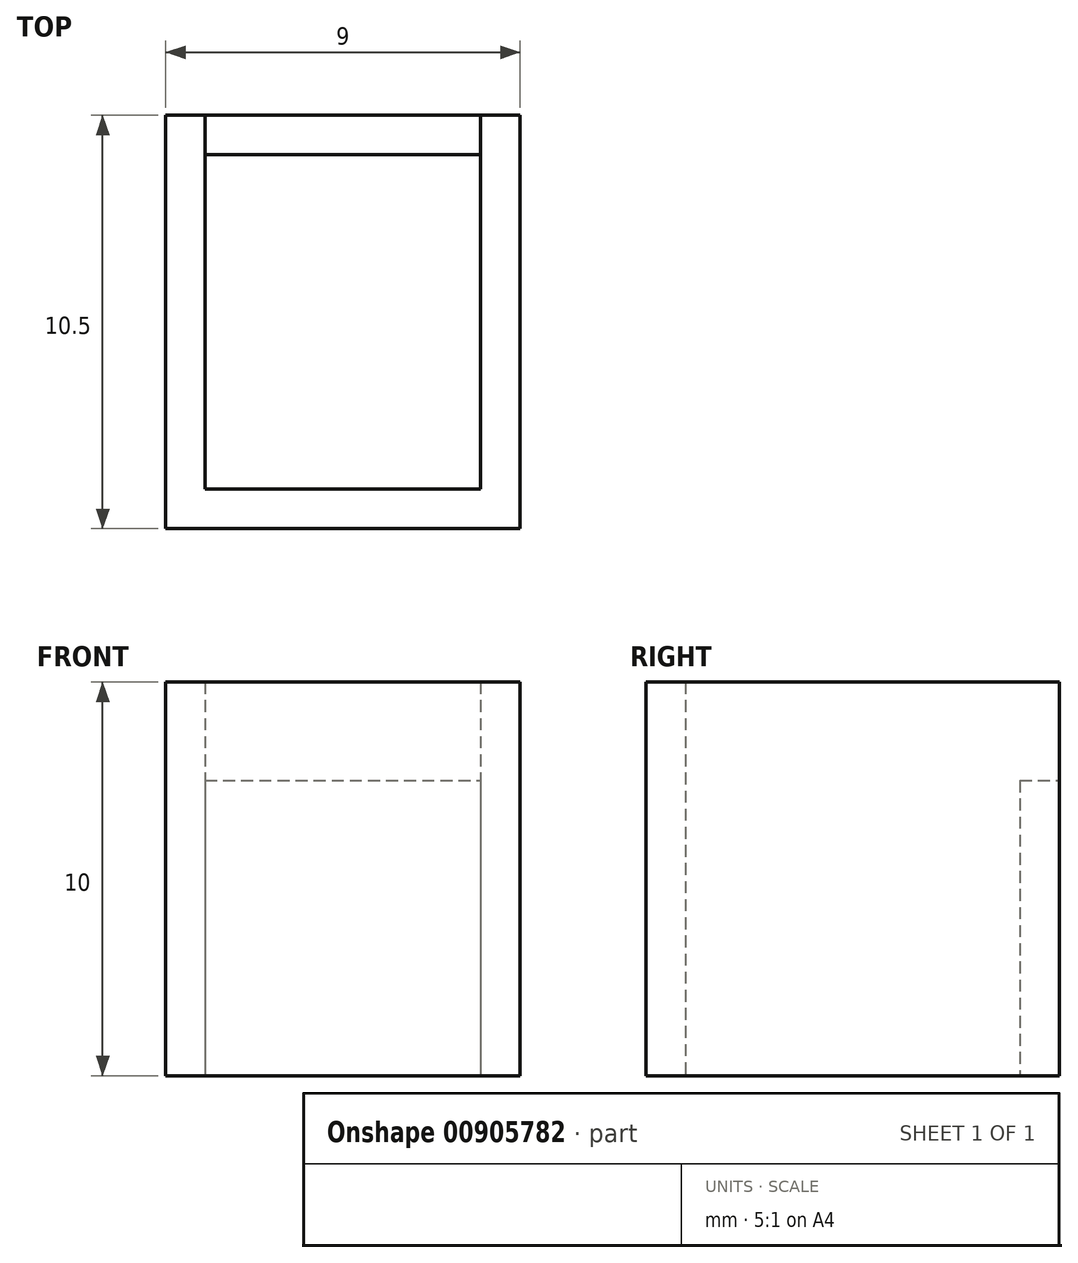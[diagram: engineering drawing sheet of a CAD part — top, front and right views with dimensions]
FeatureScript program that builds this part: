
annotation { "Feature Type Name" : "Feature", "Feature Type Description" : "" }
export const myFeature = defineFeature(function(context is Context, id is Id, definition is map)
    precondition{}
    {
        {
            var Q0;
            Q0=qCreatedBy(makeId("Top.planeOp"),FACE);
            var sketch = newSketch(context, id + "F0", { "sketchPlane" : qUnion([Q0])});
            skLineSegment(sketch, "E0.bottom", {"start": v(-3.5, 4.25) * mm, "end": v(3.5, 4.25) * mm});
            skLineSegment(sketch, "E0.top", {"start": v(-3.5, -4.25) * mm, "end": v(3.5, -4.25) * mm});
            skLineSegment(sketch, "E0.left", {"start": v(-3.5, 4.25) * mm, "end": v(-3.5, -4.25) * mm});
            skLineSegment(sketch, "E0.right", {"start": v(3.5, 4.25) * mm, "end": v(3.5, -4.25) * mm});
            skPoint(sketch, "E0.middle", {"position": v(0, 0) * mm});
            skLineSegment(sketch, "E1.0", {"start": v(-4.5, 5.25) * mm, "end": v(-4.5, -5.25) * mm});
            skLineSegment(sketch, "E1.1", {"start": v(-4.5, 5.25) * mm, "end": v(4.5, 5.25) * mm});
            skLineSegment(sketch, "E1.2", {"start": v(4.5, 5.25) * mm, "end": v(4.5, -5.25) * mm});
            skLineSegment(sketch, "E1.3", {"start": v(-4.5, -5.25) * mm, "end": v(4.5, -5.25) * mm});
            skLineSegment(sketch, "E2", {"start": v(-3.5, 4.25) * mm, "end": v(-3.5, 5.25) * mm});
            skLineSegment(sketch, "E3", {"start": v(3.5, 4.25) * mm, "end": v(3.5, 5.25) * mm});
            skSolve(sketch);
        }
        {
            var Q0;
            Q0=makeQuery(id+"F0.imprint","IMPRINT",FACE,{"disambiguationData":[TD([[makeQuery(id+"F0.imprint","IMPRINT",EDGE,{"derivedFrom":sQuery(id+"F0.wireOp",EDGE,"E0.top")}),-1.0]])]});
            extrude(context, id + "F1", {"entities" : qUnion([Q0]), "depth" : 10 * mm, "offsetDistance" : 25 * mm});
        }
        {
            var Q0;
            Q0=makeQuery(id+"F0.imprint","IMPRINT",FACE,{"disambiguationData":[TD([[makeQuery(id+"F0.imprint","IMPRINT",EDGE,{"derivedFrom":sQuery(id+"F0.wireOp",EDGE,"E0.bottom")}),1.0]])]});
            extrude(context, id + "F2", {"entities" : qUnion([Q0]), "operationType" : NewBodyOperationType.ADD, "depth" : 7.5 * mm, "offsetDistance" : 25 * mm});
        }
    });
